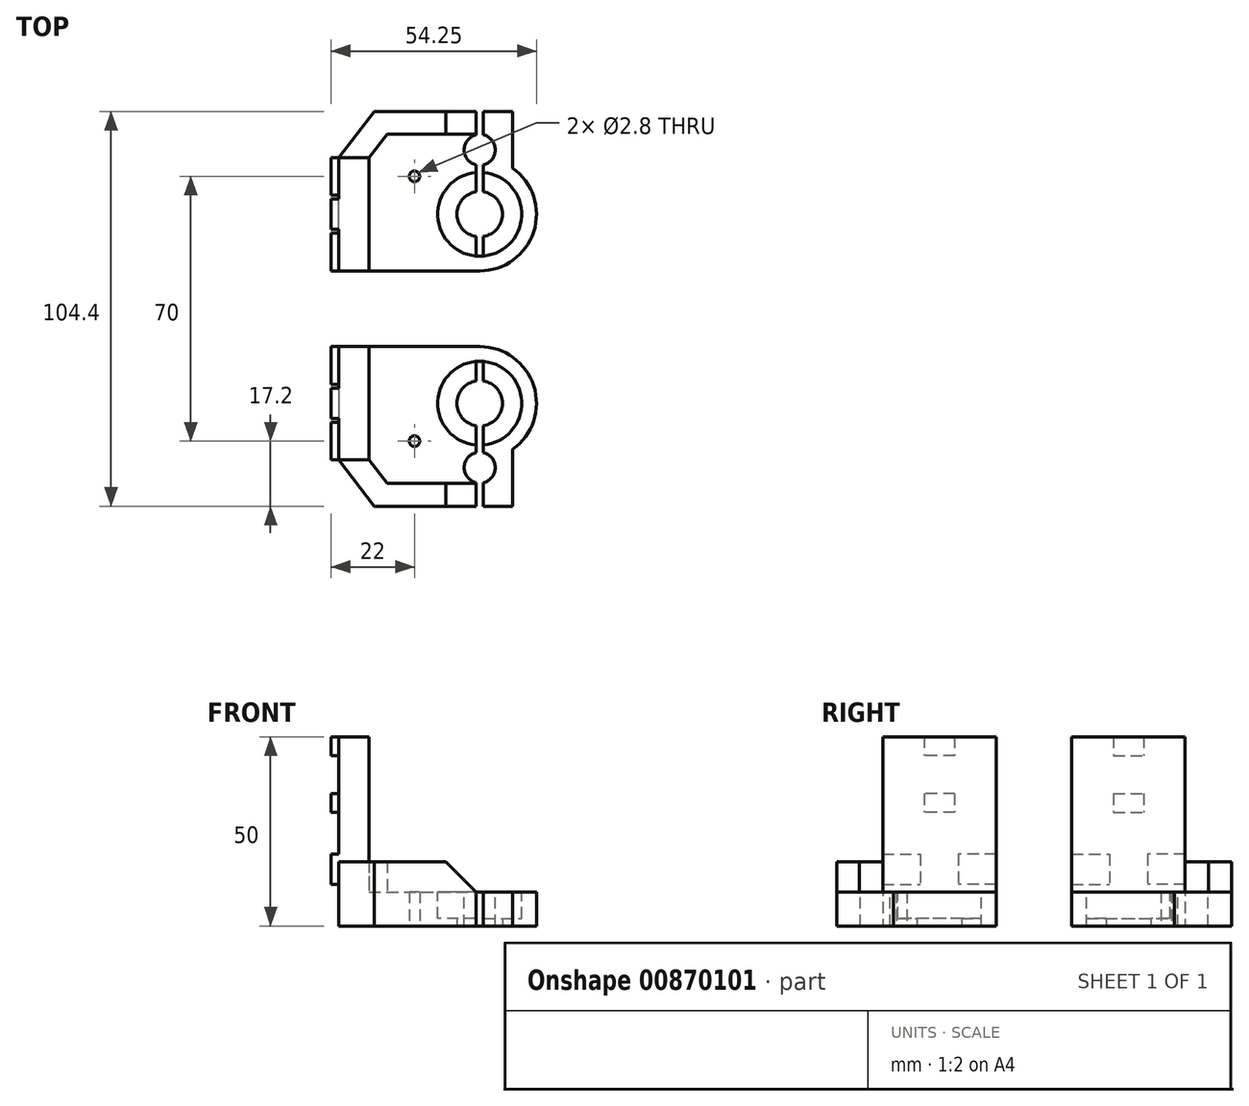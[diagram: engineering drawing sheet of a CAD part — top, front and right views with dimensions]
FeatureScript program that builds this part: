
annotation { "Feature Type Name" : "Feature", "Feature Type Description" : "" }
export const myFeature = defineFeature(function(context is Context, id is Id, definition is map)
    precondition{}
    {
        {
            var Q0;
            Q0=qCreatedBy(makeId("Top.planeOp"),FACE);
            var sketch = newSketch(context, id + "F0", { "sketchPlane" : qUnion([Q0])});
            skLineSegment(sketch, "E0", {"start": v(0, 0) * mm, "end": v(37.25, 0) * mm});
            skLineSegment(sketch, "E1", {"start": v(0, 0) * mm, "end": v(0, -30) * mm});
            skLineSegment(sketch, "E2", {"start": v(0, -30) * mm, "end": v(9.34, -42.2) * mm});
            skLineSegment(sketch, "E3", {"start": v(9.34, -42.2) * mm, "end": v(46, -42.2) * mm});
            skLineSegment(sketch, "E4", {"start": v(46, -42.2) * mm, "end": v(46, -27.18) * mm});
            skArc(sketch, "E5", {"start": v(46, -27.18) * mm, "mid": v(51.53, -10.4) * mm, "end": v(37.25, 0) * mm});
            skCircle(sketch, "E6", {"center": v(37.25, -15) * mm, "radius": 6 * mm});
            skCircle(sketch, "E7", {"center": v(20, -25) * mm, "radius": 1.4 * mm});
            skSolve(sketch);
        }
        {
            var Q0;
            Q0 = qSketchRegion(id + "F0", true);
            extrude(context, id + "F1", {"entities" : qUnion([Q0]), "depth" : 9 * mm, "offsetDistance" : 25 * mm});
        }
        {
            var Q0;
            Q0=makeQuery(id+"F1.opExtrude","CAP_FACE",FACE,{"disambiguationData":[OSD([sQuery(id+"F0.wireOp",EDGE,"E0"),sQuery(id+"F0.wireOp",EDGE,"E1"),sQuery(id+"F0.wireOp",EDGE,"E2"),sQuery(id+"F0.wireOp",EDGE,"E3"),sQuery(id+"F0.wireOp",EDGE,"E4"),sQuery(id+"F0.wireOp",EDGE,"E5"),sQuery(id+"F0.wireOp",EDGE,"E6")])],"isStart":false});
            var sketch = newSketch(context, id + "F2", { "sketchPlane" : qUnion([Q0])});
            skCircle(sketch, "E8", {"center": v(37.25, -15) * mm, "radius": 11.1 * mm});
            skSolve(sketch);
        }
        {
            var Q0;
            Q0 = qSketchRegion(id + "F2", true);
            extrude(context, id + "F3", {"entities" : qUnion([Q0]), "operationType" : NewBodyOperationType.REMOVE, "oppositeDirection" : true, "depth" : 7 * mm, "offsetDistance" : 25 * mm});
        }
        {
            var Q0;
            Q0=makeQuery(id+"F1.opExtrude","CAP_FACE",FACE,{"disambiguationData":[OSD([sQuery(id+"F0.wireOp",EDGE,"E0"),sQuery(id+"F0.wireOp",EDGE,"E1"),sQuery(id+"F0.wireOp",EDGE,"E2"),sQuery(id+"F0.wireOp",EDGE,"E3"),sQuery(id+"F0.wireOp",EDGE,"E4"),sQuery(id+"F0.wireOp",EDGE,"E5"),sQuery(id+"F0.wireOp",EDGE,"E6")])],"isStart":false});
            var sketch = newSketch(context, id + "F4", { "sketchPlane" : qUnion([Q0])});
            skLineSegment(sketch, "E9", {"start": v(37.25, -15) * mm, "end": v(37.25, -42.2) * mm, "construction": true});
            skLineSegment(sketch, "E10", {"start": v(36.25, -42.2) * mm, "end": v(38.25, -42.2) * mm});
            skLineSegment(sketch, "E11", {"start": v(38.25, -42.2) * mm, "end": v(38.25, -35.98) * mm});
            skLineSegment(sketch, "E12", {"start": v(36.25, -42.2) * mm, "end": v(36.25, -35.98) * mm});
            skArc(sketch, "E13", {"start": v(36.25, -3.95) * mm, "mid": v(37.25, -3.9) * mm, "end": v(38.25, -3.95) * mm});
            skArc(sketch, "E14", {"start": v(36.25, -28.02) * mm, "mid": v(33.15, -32) * mm, "end": v(36.25, -35.98) * mm});
            skLineSegment(sketch, "E15.trimOffspring", {"start": v(36.25, -28.02) * mm, "end": v(36.25, -3.95) * mm});
            skLineSegment(sketch, "E16.trimOffspring", {"start": v(38.25, -28.02) * mm, "end": v(38.25, -3.95) * mm});
            skArc(sketch, "E17.trimOffspring", {"start": v(38.25, -35.98) * mm, "mid": v(41.35, -32) * mm, "end": v(38.25, -28.02) * mm});
            skSolve(sketch);
        }
        {
            var Q0;
            Q0 = qSketchRegion(id + "F4", true);
            var Q1;
            Q1=makeQuery(id+"F1.opExtrude","CAP_FACE",FACE,{"disambiguationData":[OSD([sQuery(id+"F0.wireOp",EDGE,"E0"),sQuery(id+"F0.wireOp",EDGE,"E1"),sQuery(id+"F0.wireOp",EDGE,"E2"),sQuery(id+"F0.wireOp",EDGE,"E3"),sQuery(id+"F0.wireOp",EDGE,"E4"),sQuery(id+"F0.wireOp",EDGE,"E5"),sQuery(id+"F0.wireOp",EDGE,"E6")])],"isStart":true});
            extrude(context, id + "F5", {"entities" : qUnion([Q0]), "operationType" : NewBodyOperationType.REMOVE, "endBound" : BoundingType.UP_TO_SURFACE, "oppositeDirection" : true, "depth" : 25 * mm, "endBoundEntityFace" : qUnion([Q1]), "offsetDistance" : 25 * mm});
        }
        {
            var Q0;
            Q0=makeQuery(id+"F1.opExtrude","CAP_FACE",FACE,{"disambiguationData":[OSD([sQuery(id+"F0.wireOp",EDGE,"E0"),sQuery(id+"F0.wireOp",EDGE,"E1"),sQuery(id+"F0.wireOp",EDGE,"E2"),sQuery(id+"F0.wireOp",EDGE,"E3"),sQuery(id+"F0.wireOp",EDGE,"E4"),sQuery(id+"F0.wireOp",EDGE,"E5"),sQuery(id+"F0.wireOp",EDGE,"E6")])],"isStart":false});
            var sketch = newSketch(context, id + "F6", { "sketchPlane" : qUnion([Q0])});
            skLineSegment(sketch, "E18.bottom", {"start": v(0, 0) * mm, "end": v(8, 0) * mm});
            skLineSegment(sketch, "E18.top", {"start": v(0, -30) * mm, "end": v(8, -30) * mm});
            skLineSegment(sketch, "E18.left", {"start": v(0, 0) * mm, "end": v(0, -30) * mm});
            skLineSegment(sketch, "E18.right", {"start": v(8, 0) * mm, "end": v(8, -30) * mm});
            skSolve(sketch);
        }
        {
            var Q0;
            Q0 = qSketchRegion(id + "F6", true);
            extrude(context, id + "F7", {"entities" : qUnion([Q0]), "operationType" : NewBodyOperationType.ADD, "depth" : 41 * mm, "offsetDistance" : 25 * mm});
        }
        {
            var Q0;
            Q0=makeQuery(id+"F1.opExtrude","CAP_FACE",FACE,{"disambiguationData":[OSD([sQuery(id+"F0.wireOp",EDGE,"E0"),sQuery(id+"F0.wireOp",EDGE,"E1"),sQuery(id+"F0.wireOp",EDGE,"E2"),sQuery(id+"F0.wireOp",EDGE,"E3"),sQuery(id+"F0.wireOp",EDGE,"E4"),sQuery(id+"F0.wireOp",EDGE,"E5"),sQuery(id+"F0.wireOp",EDGE,"E6")])],"isStart":false});
            var sketch = newSketch(context, id + "F8", { "sketchPlane" : qUnion([Q0])});
            skLineSegment(sketch, "E19", {"start": v(0, -30) * mm, "end": v(8, -30) * mm});
            skLineSegment(sketch, "E20", {"start": v(8, -30) * mm, "end": v(12.75, -36.2) * mm});
            skLineSegment(sketch, "E21", {"start": v(12.75, -36.2) * mm, "end": v(36.25, -36.2) * mm});
            skLineSegment(sketch, "E22", {"start": v(36.25, -36.2) * mm, "end": v(36.25, -42.2) * mm});
            skLineSegment(sketch, "E23", {"start": v(36.25, -42.2) * mm, "end": v(9.34, -42.2) * mm});
            skLineSegment(sketch, "E24", {"start": v(9.34, -42.2) * mm, "end": v(0, -30) * mm});
            skSolve(sketch);
        }
        {
            var Q0;
            Q0 = qSketchRegion(id + "F8", true);
            extrude(context, id + "F9", {"entities" : qUnion([Q0]), "operationType" : NewBodyOperationType.ADD, "depth" : 8 * mm, "offsetDistance" : 25 * mm});
        }
        {
            var Q0;
            Q0=makeQuery(id+"F9.opExtrude","CAP_EDGE",EDGE,{"disambiguationData":[OSD([sQuery(id+"F8.wireOp",EDGE,"E22")])],"isStart":false});
            chamfer(context, id + "F10", {"entities" : qUnion([Q0]), "width" : 8 * mm, "tangentPropagation" : true});
        }
        {
            var Q0;
            Q0=makeQuery(id+"F7.boolean.opBoolean","MERGE",FACE,{"derivedFrom":[makeQuery(id+"F1.opExtrude","SWEPT_FACE",FACE,{"disambiguationData":[OSD([sQuery(id+"F0.wireOp",EDGE,"E1")])]}),makeQuery(id+"F7.opExtrude","SWEPT_FACE",FACE,{"disambiguationData":[OSD([sQuery(id+"F6.wireOp",EDGE,"E18.left")])]})]});
            var sketch = newSketch(context, id + "F11", { "sketchPlane" : qUnion([Q0])});
            skLineSegment(sketch, "E25.bottom", {"start": v(0, 19) * mm, "end": v(10, 19) * mm});
            skLineSegment(sketch, "E25.top", {"start": v(0, 11) * mm, "end": v(10, 11) * mm});
            skLineSegment(sketch, "E25.left", {"start": v(0, 19) * mm, "end": v(0, 11) * mm});
            skLineSegment(sketch, "E25.right", {"start": v(10, 19) * mm, "end": v(10, 11) * mm});
            skLineSegment(sketch, "E26.bottom", {"start": v(30, 19) * mm, "end": v(20, 19) * mm});
            skLineSegment(sketch, "E26.top", {"start": v(30, 11) * mm, "end": v(20, 11) * mm});
            skLineSegment(sketch, "E26.left", {"start": v(30, 19) * mm, "end": v(30, 11) * mm});
            skLineSegment(sketch, "E26.right", {"start": v(20, 19) * mm, "end": v(20, 11) * mm});
            skLineSegment(sketch, "E27.bottom", {"start": v(11, 50) * mm, "end": v(19, 50) * mm});
            skLineSegment(sketch, "E27.top", {"start": v(11, 45) * mm, "end": v(19, 45) * mm});
            skLineSegment(sketch, "E27.left", {"start": v(11, 50) * mm, "end": v(11, 45) * mm});
            skLineSegment(sketch, "E27.right", {"start": v(19, 50) * mm, "end": v(19, 45) * mm});
            skLineSegment(sketch, "E28.bottom", {"start": v(11, 35) * mm, "end": v(19, 35) * mm});
            skLineSegment(sketch, "E28.top", {"start": v(11, 30) * mm, "end": v(19, 30) * mm});
            skLineSegment(sketch, "E28.left", {"start": v(11, 35) * mm, "end": v(11, 30) * mm});
            skLineSegment(sketch, "E28.right", {"start": v(19, 35) * mm, "end": v(19, 30) * mm});
            skLineSegment(sketch, "E29", {"start": v(15, 50) * mm, "end": v(15, 0) * mm, "construction": true});
            skSolve(sketch);
        }
        {
            var Q0;
            Q0 = qSketchRegion(id + "F11", true);
            extrude(context, id + "F12", {"entities" : qUnion([Q0]), "operationType" : NewBodyOperationType.ADD, "depth" : 2 * mm, "offsetDistance" : 25 * mm});
        }
        {
            var Q0;
            Q0=makeQuery(id+"F1.opExtrude","SWEPT_BODY",BODY,{"disambiguationData":[OSD([sQuery(id+"F0.wireOp",EDGE,"E0"),sQuery(id+"F0.wireOp",EDGE,"E1"),sQuery(id+"F0.wireOp",EDGE,"E2"),sQuery(id+"F0.wireOp",EDGE,"E3"),sQuery(id+"F0.wireOp",EDGE,"E4"),sQuery(id+"F0.wireOp",EDGE,"E5"),sQuery(id+"F0.wireOp",EDGE,"E6"),sQuery(id+"F0.wireOp",EDGE,"E7")])]});
            var Q1;
            Q1=qCreatedBy(makeId("Front.planeOp"),FACE);
            mirror(context, id + "F13", {"entities" : qUnion([Q0]), "mirrorPlane" : qUnion([Q1])});
        }
        {
            var Q0;
            Q0=makeQuery(id+"F13.opPattern","COPY",BODY,{"derivedFrom":makeQuery(id+"F1.opExtrude","SWEPT_BODY",BODY,{"disambiguationData":[OSD([sQuery(id+"F0.wireOp",EDGE,"E0"),sQuery(id+"F0.wireOp",EDGE,"E1"),sQuery(id+"F0.wireOp",EDGE,"E2"),sQuery(id+"F0.wireOp",EDGE,"E3"),sQuery(id+"F0.wireOp",EDGE,"E4"),sQuery(id+"F0.wireOp",EDGE,"E5"),sQuery(id+"F0.wireOp",EDGE,"E6"),sQuery(id+"F0.wireOp",EDGE,"E7")])]}),"instanceName":"1"});
            transform(context, id + "F14", {"entities" : qUnion([Q0]), "transformType" : TransformType.TRANSLATION_3D, "dx" : 0 * mm, "dy" : 20 * mm, "dz" : 0 * mm, "makeCopy" : false});
        }
    });
